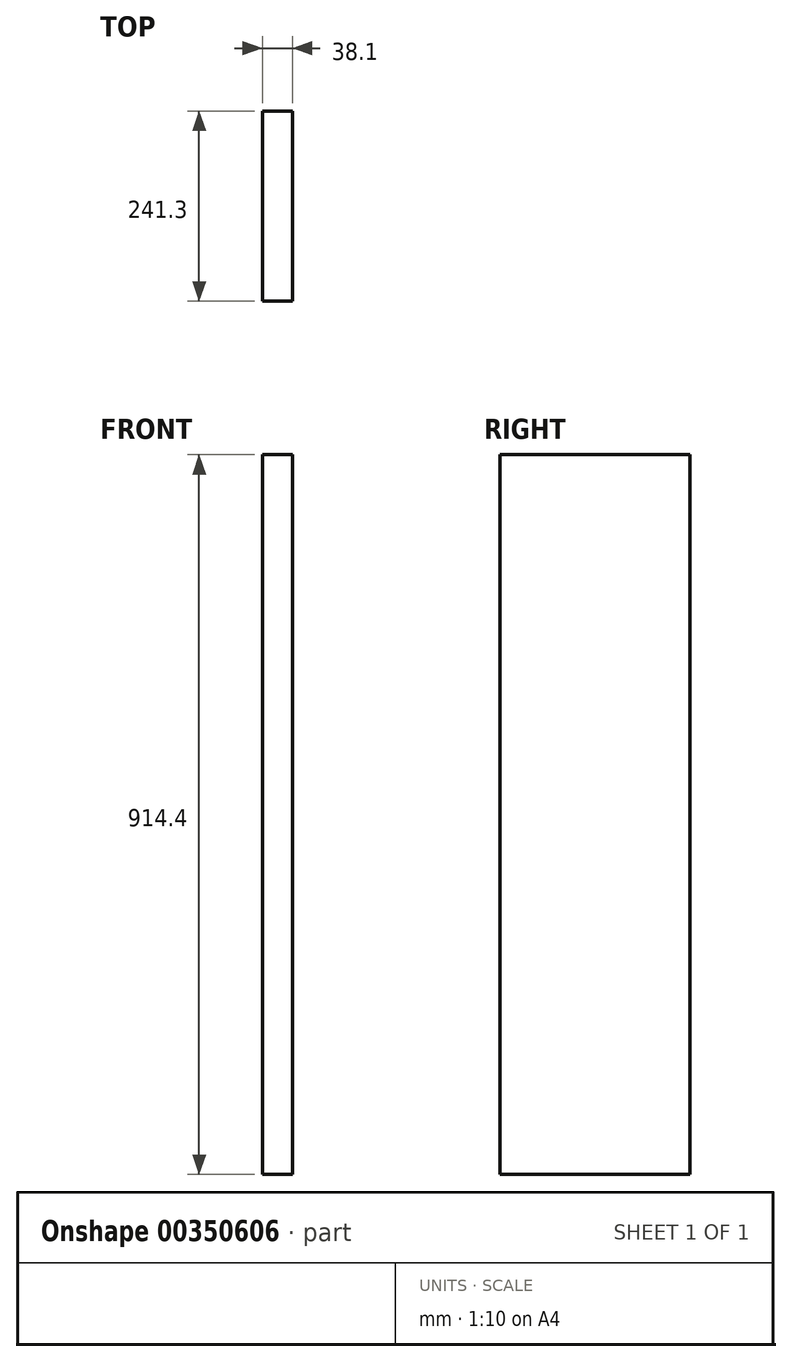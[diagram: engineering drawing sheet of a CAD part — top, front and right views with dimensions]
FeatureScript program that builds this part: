
annotation { "Feature Type Name" : "Feature", "Feature Type Description" : "" }
export const myFeature = defineFeature(function(context is Context, id is Id, definition is map)
    precondition{}
    {
        {
            var Q0;
            Q0=qCreatedBy(makeId("Top.planeOp"),FACE);
            var sketch = newSketch(context, id + "F0", { "sketchPlane" : qUnion([Q0])});
            skLineSegment(sketch, "E0.bottom", {"start": v(19.05, 120.65) * mm, "end": v(-19.05, 120.65) * mm});
            skLineSegment(sketch, "E0.top", {"start": v(19.05, -120.65) * mm, "end": v(-19.05, -120.65) * mm});
            skLineSegment(sketch, "E0.left", {"start": v(19.05, 120.65) * mm, "end": v(19.05, -120.65) * mm});
            skLineSegment(sketch, "E0.right", {"start": v(-19.05, 120.65) * mm, "end": v(-19.05, -120.65) * mm});
            skPoint(sketch, "E0.middle", {"position": v(0, 0) * mm});
            skSolve(sketch);
        }
        {
            var Q0;
            Q0=makeQuery(id+"F0.imprint","IMPRINT",FACE,{"disambiguationData":[TD([[makeQuery(id+"F0.imprint","IMPRINT",EDGE,{"derivedFrom":sQuery(id+"F0.wireOp",EDGE,"E0.bottom")}),1.0]])]});
            extrude(context, id + "F1", {"entities" : qUnion([Q0]), "depth" : 914.4 * mm});
        }
    });
